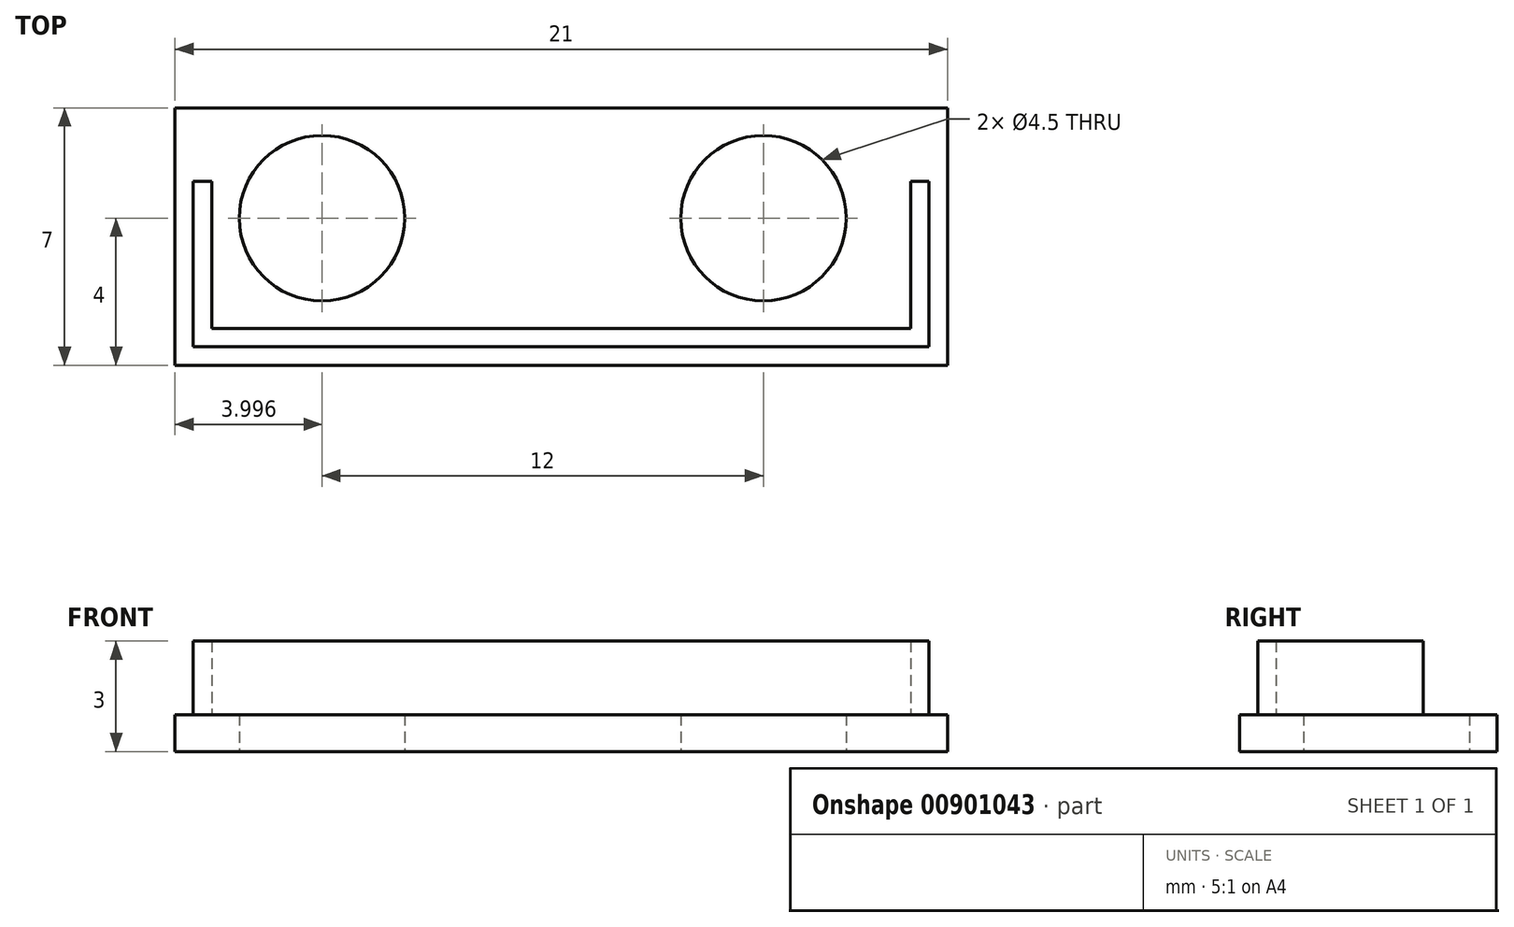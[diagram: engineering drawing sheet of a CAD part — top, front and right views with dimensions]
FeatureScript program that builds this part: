
annotation { "Feature Type Name" : "Feature", "Feature Type Description" : "" }
export const myFeature = defineFeature(function(context is Context, id is Id, definition is map)
    precondition{}
    {
        {
            var Q0;
            Q0=qCreatedBy(makeId("Top.planeOp"),FACE);
            var sketch = newSketch(context, id + "F0", { "sketchPlane" : qUnion([Q0])});
            skLineSegment(sketch, "E0", {"start": v(-12.67, 0) * mm, "end": v(10.74, 0) * mm, "construction": true});
            skLineSegment(sketch, "E1", {"start": v(6.17, 6) * mm, "end": v(6.17, -6.74) * mm, "construction": true});
            skLineSegment(sketch, "E2", {"start": v(-5.83, 6.15) * mm, "end": v(-5.83, -7.33) * mm, "construction": true});
            skLineSegment(sketch, "E3.bottom", {"start": v(-9.83, 3) * mm, "end": v(11.17, 3) * mm});
            skLineSegment(sketch, "E3.top", {"start": v(-9.83, -4) * mm, "end": v(11.17, -4) * mm});
            skLineSegment(sketch, "E3.left", {"start": v(-9.83, 3) * mm, "end": v(-9.83, -4) * mm});
            skLineSegment(sketch, "E3.right", {"start": v(11.17, 3) * mm, "end": v(11.17, -4) * mm});
            skCircle(sketch, "E4", {"center": v(6.17, 0) * mm, "radius": 2.25 * mm});
            skCircle(sketch, "E5", {"center": v(-5.83, 0) * mm, "radius": 2.25 * mm});
            skSolve(sketch);
        }
        {
            var Q0;
            Q0=makeQuery(id+"F0.imprint","IMPRINT",FACE,{"disambiguationData":[TD([[makeQuery(id+"F0.imprint","IMPRINT",EDGE,{"derivedFrom":sQuery(id+"F0.wireOp",EDGE,"E3.bottom")}),-1.0]])]});
            extrude(context, id + "F1", {"entities" : qUnion([Q0]), "depth" : 1 * mm, "offsetDistance" : 25 * mm});
        }
        {
            var Q0;
            Q0=makeQuery(id+"F1.opExtrude","CAP_FACE",FACE,{"disambiguationData":[OSD([sQuery(id+"F0.wireOp",EDGE,"E3.bottom"),sQuery(id+"F0.wireOp",EDGE,"E3.top"),sQuery(id+"F0.wireOp",EDGE,"E3.left"),sQuery(id+"F0.wireOp",EDGE,"E3.right"),sQuery(id+"F0.wireOp",EDGE,"E4"),sQuery(id+"F0.wireOp",EDGE,"E5")])],"isStart":false});
            var sketch = newSketch(context, id + "F2", { "sketchPlane" : qUnion([Q0])});
            skLineSegment(sketch, "E6", {"start": v(-8.83, 1) * mm, "end": v(-8.83, -3) * mm});
            skLineSegment(sketch, "E7", {"start": v(-8.83, -3) * mm, "end": v(10.17, -3) * mm});
            skLineSegment(sketch, "E8", {"start": v(10.17, -3) * mm, "end": v(10.17, 1) * mm});
            skLineSegment(sketch, "E9.0", {"start": v(10.67, -3.5) * mm, "end": v(10.67, 1) * mm});
            skLineSegment(sketch, "E9.1", {"start": v(-9.33, -3.5) * mm, "end": v(10.67, -3.5) * mm});
            skLineSegment(sketch, "E9.2", {"start": v(-9.33, 1) * mm, "end": v(-9.33, -3.5) * mm});
            skLineSegment(sketch, "E10", {"start": v(-8.83, 1) * mm, "end": v(-9.33, 1) * mm});
            skLineSegment(sketch, "E11", {"start": v(10.17, 1) * mm, "end": v(10.67, 1) * mm});
            skSolve(sketch);
        }
        {
            var Q0;
            Q0=makeQuery(id+"F2.imprint","IMPRINT",FACE,{"disambiguationData":[TD([[makeQuery(id+"F2.imprint","IMPRINT",EDGE,{"derivedFrom":sQuery(id+"F2.wireOp",EDGE,"E6")}),-1.0]])]});
            extrude(context, id + "F3", {"entities" : qUnion([Q0]), "operationType" : NewBodyOperationType.ADD, "depth" : 2 * mm, "offsetDistance" : 25 * mm});
        }
    });
